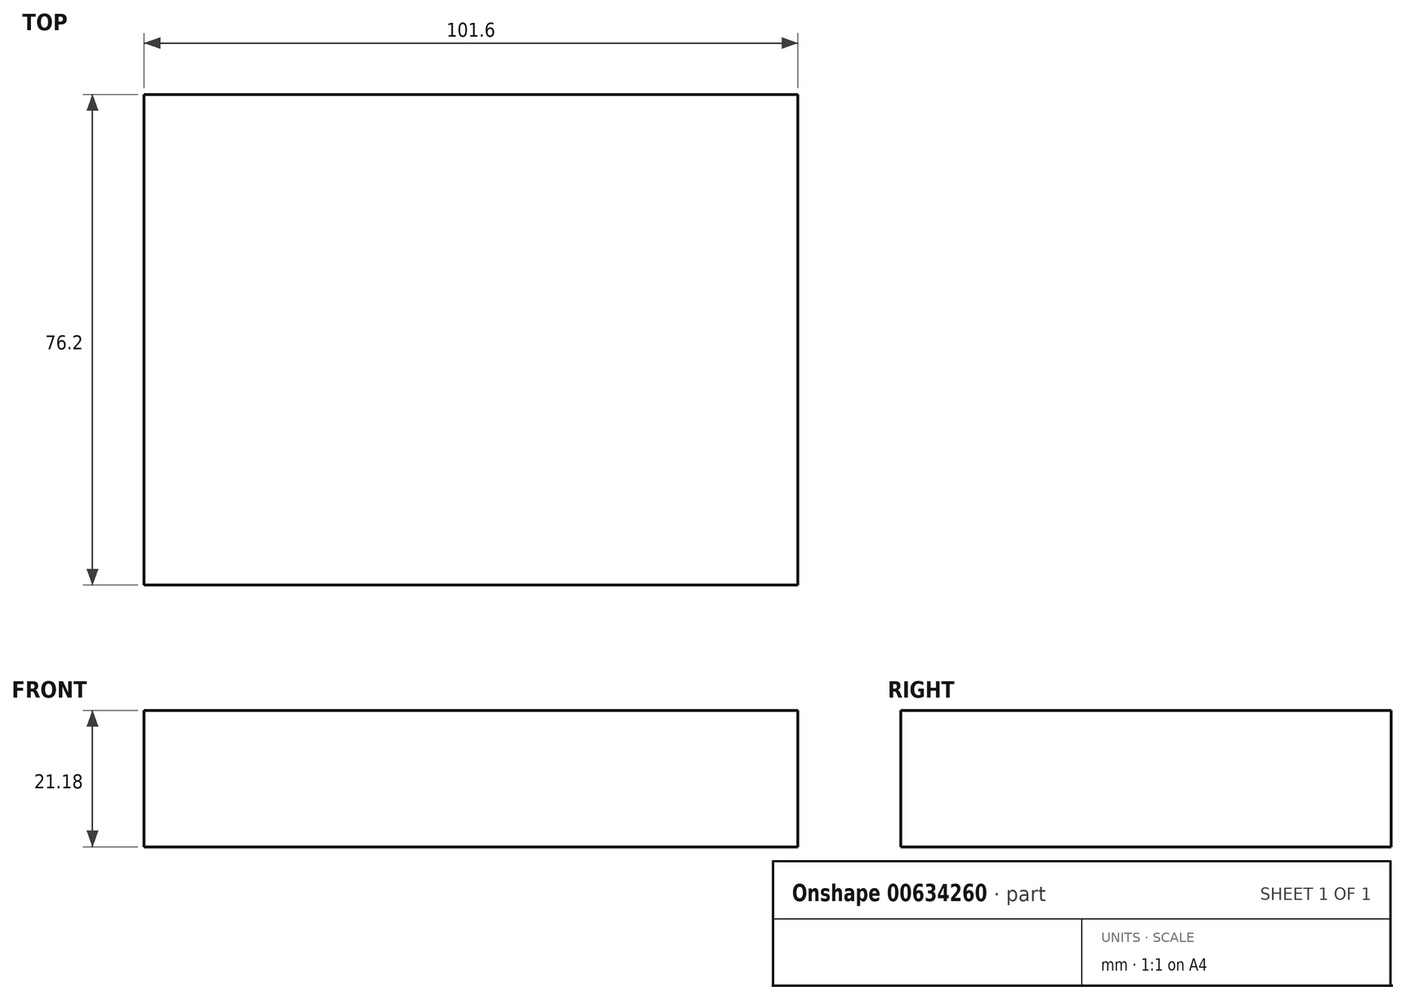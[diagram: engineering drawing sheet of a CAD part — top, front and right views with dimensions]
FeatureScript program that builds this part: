
annotation { "Feature Type Name" : "Feature", "Feature Type Description" : "" }
export const myFeature = defineFeature(function(context is Context, id is Id, definition is map)
    precondition{}
    {
        {
            var Q0;
            Q0=qCreatedBy(makeId("Front.planeOp"),FACE);
            var sketch = newSketch(context, id + "F0", { "sketchPlane" : qUnion([Q0])});
            skLineSegment(sketch, "E0.bottom", {"start": v(50.8, 10.6) * mm, "end": v(-50.8, 10.6) * mm});
            skLineSegment(sketch, "E0.top", {"start": v(50.8, -10.6) * mm, "end": v(-50.8, -10.6) * mm});
            skLineSegment(sketch, "E0.left", {"start": v(50.8, 10.6) * mm, "end": v(50.8, -10.6) * mm});
            skLineSegment(sketch, "E0.right", {"start": v(-50.8, 10.6) * mm, "end": v(-50.8, -10.6) * mm});
            skPoint(sketch, "E0.middle", {"position": v(0, 0) * mm});
            skLineSegment(sketch, "E1.bottom", {"start": v(50.8, 10.6) * mm, "end": v(-17.27, 10.6) * mm});
            skLineSegment(sketch, "E1.top", {"start": v(50.8, 31.78) * mm, "end": v(-17.27, 31.78) * mm});
            skLineSegment(sketch, "E1.left", {"start": v(50.8, 10.6) * mm, "end": v(50.8, 31.78) * mm});
            skLineSegment(sketch, "E1.right", {"start": v(-17.27, 10.6) * mm, "end": v(-17.27, 31.78) * mm});
            skLineSegment(sketch, "E2.bottom", {"start": v(50.8, 31.78) * mm, "end": v(16.76, 31.78) * mm});
            skLineSegment(sketch, "E2.top", {"start": v(50.8, 52.96) * mm, "end": v(16.76, 52.96) * mm});
            skLineSegment(sketch, "E2.left", {"start": v(50.8, 31.78) * mm, "end": v(50.8, 52.96) * mm});
            skLineSegment(sketch, "E2.right", {"start": v(16.76, 31.78) * mm, "end": v(16.76, 52.96) * mm});
            skSolve(sketch);
        }
        {
            var Q0;
            Q0=makeQuery(id+"F0.imprint","IMPRINT",FACE,{"disambiguationData":[TD([[makeQuery(id+"F0.imprint","IMPRINT",EDGE,{"derivedFrom":sQuery(id+"F0.wireOp",EDGE,"E2.bottom")}),-1.0]])]});
            var Q1;
            Q1=makeQuery(id+"F0.imprint","IMPRINT",FACE,{"disambiguationData":[TD([[makeQuery(id+"F0.imprint","IMPRINT",EDGE,{"derivedFrom":sQuery(id+"F0.wireOp",EDGE,"E1.bottom")}),-1.0]])]});
            var Q2;
            Q2=makeQuery(id+"F0.imprint","IMPRINT",FACE,{"disambiguationData":[TD([[makeQuery(id+"F0.imprint","IMPRINT",EDGE,{"derivedFrom":sQuery(id+"F0.wireOp",EDGE,"E0.bottom")}),1.0]])]});
            extrude(context, id + "F1", {"entities" : qUnion([Q0, Q1, Q2]), "endBound" : BoundingType.SYMMETRIC, "depth" : 76.2 * mm, "offsetDistance" : 25.4 * mm});
        }
    });
